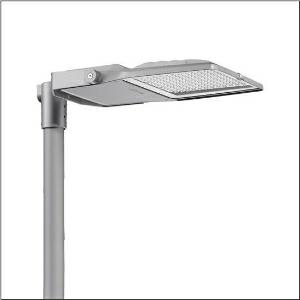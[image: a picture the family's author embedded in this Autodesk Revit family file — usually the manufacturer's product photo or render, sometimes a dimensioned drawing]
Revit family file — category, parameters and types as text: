
# Revit family: floodlight_fl_21_iq_midi___pl64_5xa7782e4e3a_6d1b
name_source: partatom
category: Lighting Fixtures
units: mm (PartAtom-declared; Revit-internal decimal feet)

## family parameters
Cut with Voids When Loaded = No
Host = Face
Light Source = No
Part Type = Normal
Room Calculation Point = No
Round Connector Dimension = Use Diameter
Shared = No

## types (1)
- --- (1 x LED, 27050 lm, 208.1 W, 4000K)
    Apparent Load = 208 VA
    CIE Flux Codes = 28 80 98 100 100
    Color Rendering = 70
    Color Temperature = 4000K
    Default Elevation = 1800 mm
    Description = Floodlight FL 21 iQ midi, floodlight, primary light control with lens, of PMMA, primary optical cover: protective disc, of toughened safety glass, transparent, light distribution: PL64, light emission: direct distribution, installation type: surface-mounted, LED, High Power LED, rated luminous flux: 27.050lm, luminous efficacy: 130lm/W, light colour: 740, colour temperature: 4000K, control gear: iQ Street-Remote/DALI, control: optimised constant luminous flux control (CLO 2.0), Desk-Remote (wireless, voltage-free reading and setting of iQ features in the workshop via application-optimized NFC function/RFID function), Smart-Wire, Night-Set, Temp-Guard, Auto-Match, Street-Remote, with terminal, 6-pole, mains connection: 220..240V, AC, 50/60Hz, start of lifetime: 208W, end of service life: 227W, reduction: 90W, luminaire housing, of diecast aluminium, powder-coated, Siteco® metallic grey (DB 702S), corrosivity category C5 mid according to DIN EN ISO 12944, suitable for swimming pools, chlorine-resistant, sealing non-destructively replaceable, please order mast flange separately, mast bracket, of steel, galvanised, powder-coated, Siteco® metallic grey (DB 702S), protection rating (complete): IP66, insulation class (complete): insulation class II (safety insulation), certification: CE, ENEC, VDE, protection symbol: D, impact resistance: IK08, permissible operating ambient temperature: -40..+40°C, permissible operating ambient temperature for outdoor applications: -40..+50°C, standard: DIN EN 12944, LABS conformity tested according to VDMA 24364:2018-05, packaging unit: 1 piece

Light Distribution: PL64
    Height = 76 mm
    Lamp = 1 x LED
    Lamp Light Flux = 27050 lm
    Lamp Power = 208.1 W
    Lamp count = 1
    Length = 657 mm
    Luminous efficacy = 130 lm/W
    Manufacturer = Siteco
    ModVariant = No
    Model = 5XA7782E4E3A
    Number of Poles = 1
    OnlyDefault = Yes
    Power Factor = 1
    Product Name = Floodlight FL 21 iQ midi | PL64
    Product group = floodlight | pylon annexe
    ProductGroupID = 6200
    Protection Class = Protection class II
    Protection Degree = IP 66
    RLX_Detail_Level = 1
    RLX_Emergency_Light_Flux = 0 lm
    RLX_Emergency_Type = 0
    RLX_Emergency_Type_DB = No
    RlxData = <blob elided: 153489 chars, md5=cbff8c57>
    Socket = socket
    Standby Power = 0 W
    System Light Flux = 27050 lm
    System Power = 208 W
    Type Comments = factory setting: luminous flux: 100 % | dim-lin: 254 | 710 mA
    Type Image = l_1007123.jpg
    URL = http://relux.com
    VarID = @adj_106982
    Voltage = 0 V
    Weight = 0.00 kg
    Width = 442 mm

## geometry (parser evidence)
native form markers: Blend x4, Sweep x12
no freeform markers — native parametric forms only
